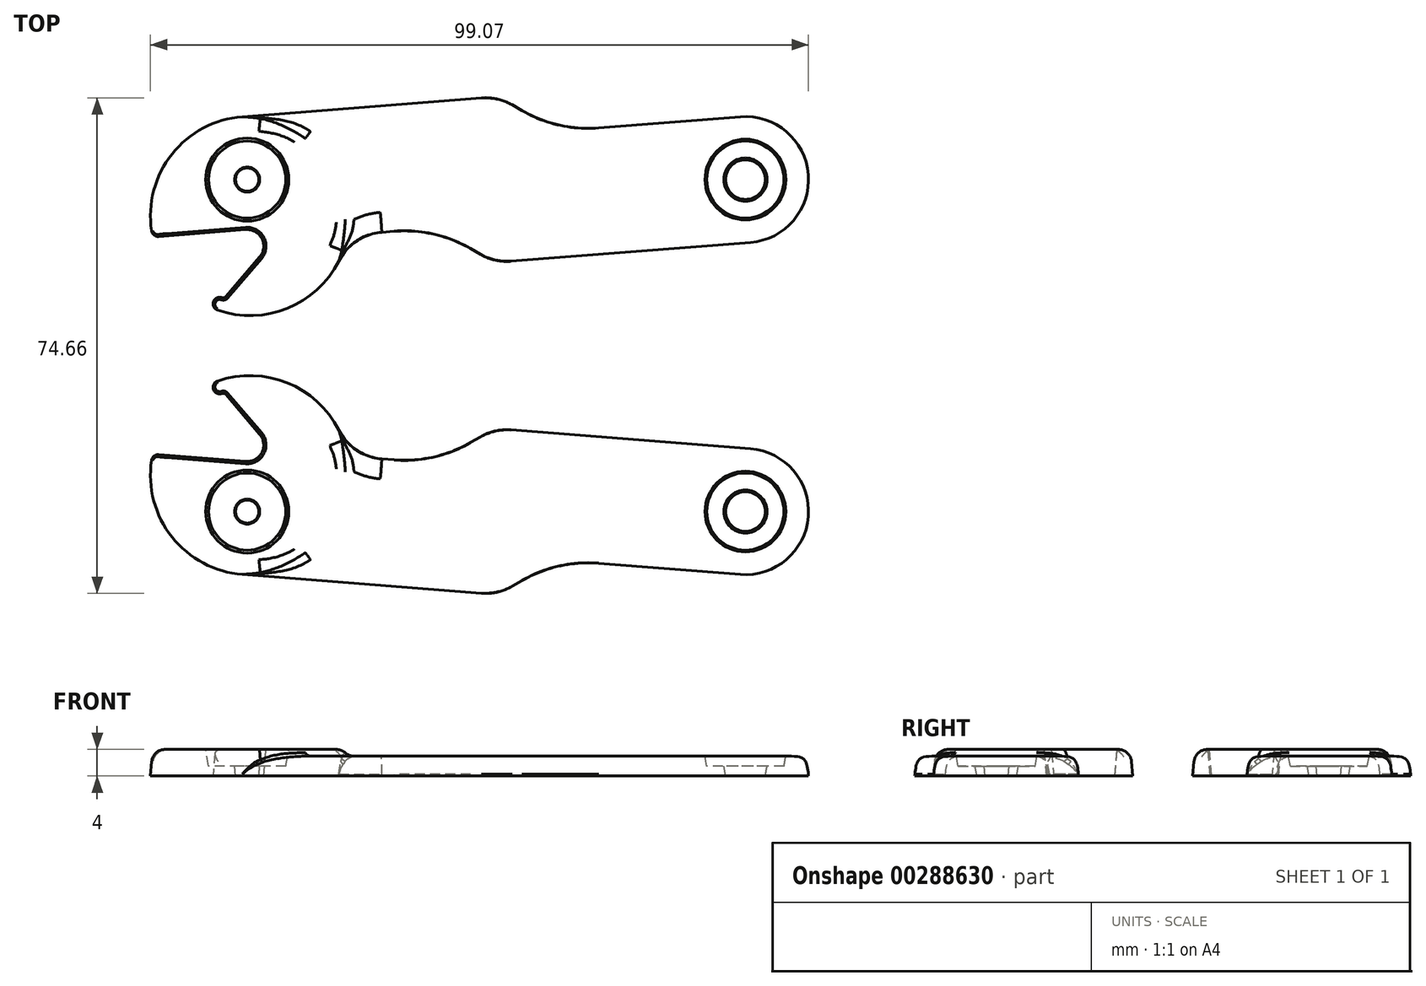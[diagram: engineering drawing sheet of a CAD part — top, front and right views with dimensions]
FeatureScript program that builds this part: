
annotation { "Feature Type Name" : "Feature", "Feature Type Description" : "" }
export const myFeature = defineFeature(function(context is Context, id is Id, definition is map)
    precondition{}
    {
        {
            var Q0;
            Q0=qCreatedBy(makeId("Top.planeOp"),FACE);
            var sketch = newSketch(context, id + "F0", { "sketchPlane" : qUnion([Q0])});
            skLineSegment(sketch, "E0", {"start": v(0, 0) * mm, "end": v(75, 0) * mm, "construction": true});
            skLineSegment(sketch, "E1", {"start": v(0, 0) * mm, "end": v(33, 2.6) * mm, "construction": true});
            skLineSegment(sketch, "E2", {"start": v(33, 2.6) * mm, "end": v(37.5, 0) * mm, "construction": true});
            skLineSegment(sketch, "E3", {"start": v(37.5, 0) * mm, "end": v(42, -2.6) * mm, "construction": true});
            skLineSegment(sketch, "E4", {"start": v(42, -2.6) * mm, "end": v(75, 0) * mm, "construction": true});
            skCircle(sketch, "E5", {"center": v(0, 0) * mm, "radius": 9.5 * mm, "construction": true});
            skArc(sketch, "E6", {"start": v(65.5, 0) * mm, "mid": v(81.98, -6.45) * mm, "end": v(74.25, 9.47) * mm});
            skLineSegment(sketch, "E7", {"start": v(-20.76, 0) * mm, "end": v(97.46, 0) * mm, "construction": true});
            skPoint(sketch, "E8", {"position": v(-9.5, 0) * mm});
            skPoint(sketch, "E9", {"position": v(84.5, 0) * mm});
            skLineSegment(sketch, "E10", {"start": v(0, 0) * mm, "end": v(-0.75, 9.47) * mm, "construction": true});
            skLineSegment(sketch, "E11", {"start": v(-0.75, 9.47) * mm, "end": v(37.75, 12.5) * mm});
            skLineSegment(sketch, "E12", {"start": v(37.75, 12.5) * mm, "end": v(46.74, 7.3) * mm});
            skLineSegment(sketch, "E13", {"start": v(46.74, 7.3) * mm, "end": v(74.25, 9.47) * mm});
            skLineSegment(sketch, "E14", {"start": v(0.75, -9.47) * mm, "end": v(28.26, -7.3) * mm});
            skLineSegment(sketch, "E15", {"start": v(28.26, -7.3) * mm, "end": v(37.25, -12.5) * mm});
            skLineSegment(sketch, "E16", {"start": v(37.25, -12.5) * mm, "end": v(75.75, -9.47) * mm});
            skLineSegment(sketch, "E17", {"start": v(37.75, 12.5) * mm, "end": v(28.26, -7.3) * mm, "construction": true});
            skLineSegment(sketch, "E18", {"start": v(46.74, 7.3) * mm, "end": v(37.25, -12.5) * mm, "construction": true});
            skCircle(sketch, "E19", {"center": v(0, 0) * mm, "radius": 1.75 * mm});
            skCircle(sketch, "E20", {"center": v(75, 0) * mm, "radius": 1.75 * mm});
            skLineSegment(sketch, "E21", {"start": v(0, 0) * mm, "end": v(1.6, -20.44) * mm, "construction": true});
            skArc(sketch, "E22", {"start": v(-0.75, 9.47) * mm, "mid": v(-11.32, 3.84) * mm, "end": v(-14.4, -7.73) * mm});
            skArc(sketch, "E23", {"start": v(1.6, -20.44) * mm, "mid": v(10.42, -16.67) * mm, "end": v(15.16, -8.34) * mm});
            skLineSegment(sketch, "E24", {"start": v(75, 0) * mm, "end": v(73.8, 15.34) * mm, "construction": true});
            skLineSegment(sketch, "E25", {"start": v(-3.23, -17.64) * mm, "end": v(1.88, -11.66) * mm});
            skLineSegment(sketch, "E26", {"start": v(-0.22, -7.54) * mm, "end": v(-13.33, -8.57) * mm});
            skLineSegment(sketch, "E27", {"start": v(-4.27, -18.86) * mm, "end": v(-6.06, -19) * mm, "construction": true});
            skArc(sketch, "E28", {"start": v(1.88, -11.66) * mm, "mid": v(2.2, -8.9) * mm, "end": v(-0.22, -7.54) * mm});
            skArc(sketch, "E29.trimOffspring", {"start": v(-4.47, -19.66) * mm, "mid": v(-1.47, -20.36) * mm, "end": v(1.6, -20.44) * mm});
            skPoint(sketch, "E30.visualSharp", {"position": v(-14.23, -8.64) * mm});
            skArc(sketch, "E30.filletArc", {"start": v(-14.4, -7.73) * mm, "mid": v(-14.03, -8.36) * mm, "end": v(-13.33, -8.57) * mm});
            skArc(sketch, "E31", {"start": v(-3.79, -17.78) * mm, "mid": v(-5.09, -18.37) * mm, "end": v(-4.47, -19.66) * mm});
            skArc(sketch, "E32.filletArc", {"start": v(-3.79, -17.78) * mm, "mid": v(-3.49, -17.8) * mm, "end": v(-3.23, -17.64) * mm});
            skSolve(sketch);
        }
        {
            var Q0;
            Q0=makeQuery(id+"F0.imprint","IMPRINT",FACE,{"disambiguationData":[TD([[makeQuery(id+"F0.imprint","IMPRINT",EDGE,{"derivedFrom":sQuery(id+"F0.wireOp",EDGE,"E19")}),-1.0]])]});
            var Q1;
            {var subQ6=sQuery(id+"F0.wireOp",EDGE,"E11");Q1=makeQuery(id+"F0.imprint","IMPRINT",FACE,{"disambiguationData":[TD([[makeQuery(id+"F0.imprint","IMPRINT",EDGE,{"derivedFrom":subQ6}),-1.0]])]});}
            var Q2;
            Q2=makeQuery(id+"F0.imprint","IMPRINT",FACE,{"disambiguationData":[TD([[makeQuery(id+"F0.imprint","IMPRINT",EDGE,{"derivedFrom":sQuery(id+"F0.wireOp",EDGE,"E20")}),-1.0]])]});
            var Q3;
            {var subQ1=sQuery(id+"F0.wireOp",EDGE,"E23");Q3=makeQuery(id+"F0.imprint","IMPRINT",FACE,{"disambiguationData":[TD([[makeQuery(id+"F0.imprint","IMPRINT",EDGE,{"derivedFrom":subQ1}),1.0]])]});}
            extrude(context, id + "F1", {"entities" : qUnion([Q0, Q1, Q2, Q3]), "depth" : 3 * mm, "hasDraft" : true, "draftAngle" : 5 * degree, "draftPullDirection" : true});
        }
        {
            var Q0;
            Q0=makeQuery(id+"F1.opExtrude","CAP_FACE",FACE,{"disambiguationData":[OSD([sQuery(id+"F0.wireOp",EDGE,"E6"),sQuery(id+"F0.wireOp",EDGE,"E11"),sQuery(id+"F0.wireOp",EDGE,"E12"),sQuery(id+"F0.wireOp",EDGE,"E13"),sQuery(id+"F0.wireOp",EDGE,"E14"),sQuery(id+"F0.wireOp",EDGE,"E15"),sQuery(id+"F0.wireOp",EDGE,"E16"),sQuery(id+"F0.wireOp",EDGE,"E19"),sQuery(id+"F0.wireOp",EDGE,"E20"),sQuery(id+"F0.wireOp",EDGE,"E22"),sQuery(id+"F0.wireOp",EDGE,"E23"),sQuery(id+"F0.wireOp",EDGE,"E25"),sQuery(id+"F0.wireOp",EDGE,"E26"),sQuery(id+"F0.wireOp",EDGE,"E28"),sQuery(id+"F0.wireOp",EDGE,"E29.trimOffspring"),sQuery(id+"F0.wireOp",EDGE,"E30.filletArc"),sQuery(id+"F0.wireOp",EDGE,"E31"),sQuery(id+"F0.wireOp",EDGE,"E32.filletArc")])],"isStart":false});
            var sketch = newSketch(context, id + "F2", { "sketchPlane" : qUnion([Q0])});
            skArc(sketch, "E33.0", {"start": v(-0.72, 9.2) * mm, "mid": v(-11.1, 3.68) * mm, "end": v(-14.14, -7.69) * mm});
            skArc(sketch, "E34.0", {"start": v(-14.14, -7.69) * mm, "mid": v(-13.87, -8.15) * mm, "end": v(-13.35, -8.31) * mm});
            skLineSegment(sketch, "E35.0", {"start": v(-0.24, -7.28) * mm, "end": v(-13.35, -8.31) * mm});
            skArc(sketch, "E36.0", {"start": v(2.08, -11.83) * mm, "mid": v(2.44, -8.78) * mm, "end": v(-0.24, -7.28) * mm});
            skLineSegment(sketch, "E37.0", {"start": v(-3.03, -17.8) * mm, "end": v(2.08, -11.83) * mm});
            skArc(sketch, "E38.0", {"start": v(-3.88, -18.02) * mm, "mid": v(-3.42, -18.05) * mm, "end": v(-3.03, -17.8) * mm});
            skArc(sketch, "E39.0", {"start": v(-3.88, -18.02) * mm, "mid": v(-4.84, -18.46) * mm, "end": v(-4.39, -19.41) * mm});
            skArc(sketch, "E40.0", {"start": v(-4.39, -19.41) * mm, "mid": v(7.88, -18.2) * mm, "end": v(14.94, -8.1) * mm});
            skArc(sketch, "E41", {"start": v(14.94, -8.1) * mm, "mid": v(11.36, 4.4) * mm, "end": v(-0.72, 9.2) * mm});
            skCircle(sketch, "E42.0", {"center": v(0, 0) * mm, "radius": 2.01 * mm});
            skSolve(sketch);
        }
        {
            var Q0;
            Q0=makeQuery(id+"F2.imprint","IMPRINT",FACE,{"disambiguationData":[TD([[makeQuery(id+"F2.imprint","IMPRINT",EDGE,{"derivedFrom":sQuery(id+"F2.wireOp",EDGE,"E33.0")}),1.0]])]});
            extrude(context, id + "F3", {"entities" : qUnion([Q0]), "operationType" : NewBodyOperationType.ADD, "depth" : 1 * mm, "hasDraft" : true, "draftAngle" : 5 * degree, "draftPullDirection" : true});
        }
        {
            var Q0;
            Q0=makeQuery(id+"F1.opExtrude","SWEPT_EDGE",EDGE,{"disambiguationData":[OSD([sQuery(id+"F0.wireOp",EDGE,"E14"),sQuery(id+"F0.wireOp",EDGE,"E15")])]});
            var Q1;
            Q1=makeQuery(id+"F1.opExtrude","SWEPT_EDGE",EDGE,{"disambiguationData":[OSD([sQuery(id+"F0.wireOp",EDGE,"E12"),sQuery(id+"F0.wireOp",EDGE,"E13")])]});
            fillet(context, id + "F4", {"entities" : qUnion([Q0, Q1]), "radius" : 20 * mm, "tangentPropagation" : true, "allowEdgeOverflow" : false});
        }
        {
            var Q0;
            Q0=makeQuery(id+"F1.opExtrude","SWEPT_EDGE",EDGE,{"disambiguationData":[OSD([sQuery(id+"F0.wireOp",EDGE,"E15"),sQuery(id+"F0.wireOp",EDGE,"SqaIxqJO-ytxu-bZqI-R6YT-mtZTRHwnqRUN")])]});
            var Q1;
            Q1=makeQuery(id+"F1.opExtrude","SWEPT_EDGE",EDGE,{"disambiguationData":[OSD([sQuery(id+"F0.wireOp",EDGE,"E15"),sQuery(id+"F0.wireOp",EDGE,"E16"),sQuery(id+"F0.wireOp",EDGE,"lhk9fa26-wqfy-sZaL-4qO0-kv8s20DjAP29")])]});
            var Q2;
            Q2=makeQuery(id+"F1.opExtrude","SWEPT_EDGE",EDGE,{"disambiguationData":[OSD([sQuery(id+"F0.wireOp",EDGE,"E11"),sQuery(id+"F0.wireOp",EDGE,"E12"),sQuery(id+"F0.wireOp",EDGE,"wIxREe3L-jgZz-AHNr-Kjfd-UXy7v7bFKsdN")])]});
            var Q3;
            Q3=makeQuery(id+"F1.opExtrude","SWEPT_EDGE",EDGE,{"disambiguationData":[OSD([sQuery(id+"F0.wireOp",EDGE,"E12"),sQuery(id+"F0.wireOp",EDGE,"acZJjbYW-XDDZ-AgQl-pZYt-mpwuyaKnzyxR")])]});
            var Q4;
            Q4=makeQuery(id+"F1.opExtrude","SWEPT_EDGE",EDGE,{"disambiguationData":[OSD([sQuery(id+"F0.wireOp",EDGE,"E14"),sQuery(id+"F0.wireOp",EDGE,"E23")])]});
            fillet(context, id + "F5", {"entities" : qUnion([Q0, Q1, Q2, Q3, Q4]), "radius" : 8 * mm, "tangentPropagation" : true, "allowEdgeOverflow" : false});
        }
        {
            var Q0;
            Q0=makeQuery(id+"F3.opExtrude","CAP_FACE",FACE,{"disambiguationData":[OSD([sQuery(id+"F2.wireOp",EDGE,"E33.0"),sQuery(id+"F2.wireOp",EDGE,"E34.0"),sQuery(id+"F2.wireOp",EDGE,"E35.0"),sQuery(id+"F2.wireOp",EDGE,"E36.0"),sQuery(id+"F2.wireOp",EDGE,"E37.0"),sQuery(id+"F2.wireOp",EDGE,"E38.0"),sQuery(id+"F2.wireOp",EDGE,"E39.0"),sQuery(id+"F2.wireOp",EDGE,"E40.0"),sQuery(id+"F2.wireOp",EDGE,"E41"),sQuery(id+"F2.wireOp",EDGE,"E42.0")])],"isStart":false});
            var sketch = newSketch(context, id + "F6", { "sketchPlane" : qUnion([Q0])});
            skCircle(sketch, "E43", {"center": v(0, 0) * mm, "radius": 3.5 * mm});
            skCircle(sketch, "E44", {"center": v(75, 0) * mm, "radius": 3.5 * mm});
            skLineSegment(sketch, "E45.bottom", {"start": v(-3, 3.5) * mm, "end": v(3, 3.5) * mm, "construction": true});
            skLineSegment(sketch, "E45.top", {"start": v(-3, -3.5) * mm, "end": v(3, -3.5) * mm, "construction": true});
            skLineSegment(sketch, "E45.left", {"start": v(-3, 3.5) * mm, "end": v(-3, -3.5) * mm});
            skLineSegment(sketch, "E45.right", {"start": v(3, 3.5) * mm, "end": v(3, -3.5) * mm});
            skLineSegment(sketch, "E46", {"start": v(-3, 3.5) * mm, "end": v(3, -3.5) * mm, "construction": true});
            skLineSegment(sketch, "E47.bottom", {"start": v(71.5, 3) * mm, "end": v(78.5, 3) * mm});
            skLineSegment(sketch, "E47.top", {"start": v(71.5, -3) * mm, "end": v(78.5, -3) * mm});
            skLineSegment(sketch, "E47.left", {"start": v(71.5, 3) * mm, "end": v(71.5, -3) * mm, "construction": true});
            skLineSegment(sketch, "E47.right", {"start": v(78.5, 3) * mm, "end": v(78.5, -3) * mm, "construction": true});
            skLineSegment(sketch, "E48", {"start": v(71.5, 3) * mm, "end": v(78.5, -3) * mm, "construction": true});
            skCircle(sketch, "E49.0", {"center": v(0, 0) * mm, "radius": 2.1 * mm});
            skSolve(sketch);
        }
        {
            var Q0;
            Q0=makeQuery(id+"F6.imprint","IMPRINT",FACE,{"disambiguationData":[TD([[makeQuery(id+"F6.imprint","IMPRINT",EDGE,{"derivedFrom":sQuery(id+"F6.wireOp",EDGE,"E49.0")}),-1.0]])]});
            var Q1;
            {var subQ0=sQuery(id+"F6.wireOp",EDGE,"E47.bottom");var subQ1=sQuery(id+"F6.wireOp",EDGE,"E44");var subQ2=makeQuery(id+"F6.imprint","INTERSECT",VERTEX,{"disambiguationData":[OD(0.0)],"derivedFrom":[subQ1,subQ0]});Q1=makeQuery(id+"F6.imprint","IMPRINT",FACE,{"disambiguationData":[TD([[makeQuery(id+"F6.imprint","IMPRINT",EDGE,{"disambiguationData":[TD([[subQ2,-1.0]])],"derivedFrom":subQ1}),1.0]])]});}
            extrude(context, id + "F7", {"entities" : qUnion([Q0, Q1]), "operationType" : NewBodyOperationType.REMOVE, "oppositeDirection" : true, "depth" : 2.5 * mm, "hasSecondDirection" : true, "secondDirectionBound" : SecondDirectionBoundingType.THROUGH_ALL, "secondDirectionOppositeDirection" : false, "secondDirectionDepth" : 25 * mm});
        }
        {
            var Q0;
            Q0=makeQuery(id+"F1.opExtrude","CAP_EDGE",EDGE,{"disambiguationData":[OSD([sQuery(id+"F0.wireOp",EDGE,"E14")])],"isStart":false});
            var Q1;
            Q1=makeQuery(id+"F1.opExtrude","CAP_EDGE",EDGE,{"disambiguationData":[OSD([sQuery(id+"F0.wireOp",EDGE,"E22")])],"isStart":false});
            var Q2;
            Q2=makeQuery(id+"F1.opExtrude","CAP_EDGE",EDGE,{"disambiguationData":[OSD([sQuery(id+"F0.wireOp",EDGE,"E11")])],"isStart":false});
            var Q3;
            {var subQ0=sQuery(id+"F0.wireOp",EDGE,"E12");var subQ1=sQuery(id+"F0.wireOp",EDGE,"E11");Q3=makeQuery(id+"F5.opFillet","BLEND_EDGE",EDGE,{"blendedFrom":[makeQuery(id+"F1.opExtrude","SWEPT_EDGE",EDGE,{"disambiguationData":[OSD([subQ1,subQ0])]}),makeQuery(id+"F1.opExtrude","CAP_FACE",FACE,{"disambiguationData":[OSD([sQuery(id+"F0.wireOp",EDGE,"E6"),subQ1,subQ0,sQuery(id+"F0.wireOp",EDGE,"E13"),sQuery(id+"F0.wireOp",EDGE,"E14"),sQuery(id+"F0.wireOp",EDGE,"E15"),sQuery(id+"F0.wireOp",EDGE,"E16"),sQuery(id+"F0.wireOp",EDGE,"E19"),sQuery(id+"F0.wireOp",EDGE,"E20"),sQuery(id+"F0.wireOp",EDGE,"E22"),sQuery(id+"F0.wireOp",EDGE,"E23"),sQuery(id+"F0.wireOp",EDGE,"E25"),sQuery(id+"F0.wireOp",EDGE,"E26"),sQuery(id+"F0.wireOp",EDGE,"E28"),sQuery(id+"F0.wireOp",EDGE,"E29.trimOffspring"),sQuery(id+"F0.wireOp",EDGE,"E30.filletArc"),sQuery(id+"F0.wireOp",EDGE,"E31"),sQuery(id+"F0.wireOp",EDGE,"E32.filletArc")])],"isStart":false})],"blendedInto":[makeQuery(id+"F1.opExtrude","CAP_FACE",FACE,{"disambiguationData":[OSD([sQuery(id+"F0.wireOp",EDGE,"E6"),subQ1,subQ0,sQuery(id+"F0.wireOp",EDGE,"E13"),sQuery(id+"F0.wireOp",EDGE,"E14"),sQuery(id+"F0.wireOp",EDGE,"E15"),sQuery(id+"F0.wireOp",EDGE,"E16"),sQuery(id+"F0.wireOp",EDGE,"E19"),sQuery(id+"F0.wireOp",EDGE,"E20"),sQuery(id+"F0.wireOp",EDGE,"E22"),sQuery(id+"F0.wireOp",EDGE,"E23"),sQuery(id+"F0.wireOp",EDGE,"E25"),sQuery(id+"F0.wireOp",EDGE,"E26"),sQuery(id+"F0.wireOp",EDGE,"E28"),sQuery(id+"F0.wireOp",EDGE,"E29.trimOffspring"),sQuery(id+"F0.wireOp",EDGE,"E30.filletArc"),sQuery(id+"F0.wireOp",EDGE,"E31"),sQuery(id+"F0.wireOp",EDGE,"E32.filletArc")])],"isStart":false})]});}
            var Q4;
            Q4=makeQuery(id+"F1.opExtrude","CAP_EDGE",EDGE,{"disambiguationData":[OSD([sQuery(id+"F0.wireOp",EDGE,"E12")])],"isStart":false});
            var Q5;
            {var subQ0=sQuery(id+"F0.wireOp",EDGE,"E13");var subQ1=sQuery(id+"F0.wireOp",EDGE,"E12");Q5=makeQuery(id+"F4.opFillet","BLEND_EDGE",EDGE,{"blendedFrom":[makeQuery(id+"F1.opExtrude","SWEPT_EDGE",EDGE,{"disambiguationData":[OSD([subQ1,subQ0])]}),makeQuery(id+"F1.opExtrude","CAP_FACE",FACE,{"disambiguationData":[OSD([sQuery(id+"F0.wireOp",EDGE,"E6"),sQuery(id+"F0.wireOp",EDGE,"E11"),subQ1,subQ0,sQuery(id+"F0.wireOp",EDGE,"E14"),sQuery(id+"F0.wireOp",EDGE,"E15"),sQuery(id+"F0.wireOp",EDGE,"E16"),sQuery(id+"F0.wireOp",EDGE,"E19"),sQuery(id+"F0.wireOp",EDGE,"E20"),sQuery(id+"F0.wireOp",EDGE,"E22"),sQuery(id+"F0.wireOp",EDGE,"E23"),sQuery(id+"F0.wireOp",EDGE,"E25"),sQuery(id+"F0.wireOp",EDGE,"E26"),sQuery(id+"F0.wireOp",EDGE,"E28"),sQuery(id+"F0.wireOp",EDGE,"E29.trimOffspring"),sQuery(id+"F0.wireOp",EDGE,"E30.filletArc"),sQuery(id+"F0.wireOp",EDGE,"E31"),sQuery(id+"F0.wireOp",EDGE,"E32.filletArc")])],"isStart":false})],"blendedInto":[makeQuery(id+"F1.opExtrude","CAP_FACE",FACE,{"disambiguationData":[OSD([sQuery(id+"F0.wireOp",EDGE,"E6"),sQuery(id+"F0.wireOp",EDGE,"E11"),subQ1,subQ0,sQuery(id+"F0.wireOp",EDGE,"E14"),sQuery(id+"F0.wireOp",EDGE,"E15"),sQuery(id+"F0.wireOp",EDGE,"E16"),sQuery(id+"F0.wireOp",EDGE,"E19"),sQuery(id+"F0.wireOp",EDGE,"E20"),sQuery(id+"F0.wireOp",EDGE,"E22"),sQuery(id+"F0.wireOp",EDGE,"E23"),sQuery(id+"F0.wireOp",EDGE,"E25"),sQuery(id+"F0.wireOp",EDGE,"E26"),sQuery(id+"F0.wireOp",EDGE,"E28"),sQuery(id+"F0.wireOp",EDGE,"E29.trimOffspring"),sQuery(id+"F0.wireOp",EDGE,"E30.filletArc"),sQuery(id+"F0.wireOp",EDGE,"E31"),sQuery(id+"F0.wireOp",EDGE,"E32.filletArc")])],"isStart":false})]});}
            var Q6;
            {var subQ0=sQuery(id+"F0.wireOp",EDGE,"E23");var subQ1=sQuery(id+"F0.wireOp",EDGE,"E14");Q6=makeQuery(id+"F5.opFillet","BLEND_EDGE",EDGE,{"blendedFrom":[makeQuery(id+"F1.opExtrude","SWEPT_EDGE",EDGE,{"disambiguationData":[OSD([subQ1,subQ0])]}),makeQuery(id+"F1.opExtrude","CAP_FACE",FACE,{"disambiguationData":[OSD([sQuery(id+"F0.wireOp",EDGE,"E6"),sQuery(id+"F0.wireOp",EDGE,"E11"),sQuery(id+"F0.wireOp",EDGE,"E12"),sQuery(id+"F0.wireOp",EDGE,"E13"),subQ1,sQuery(id+"F0.wireOp",EDGE,"E15"),sQuery(id+"F0.wireOp",EDGE,"E16"),sQuery(id+"F0.wireOp",EDGE,"E19"),sQuery(id+"F0.wireOp",EDGE,"E20"),sQuery(id+"F0.wireOp",EDGE,"E22"),subQ0,sQuery(id+"F0.wireOp",EDGE,"E25"),sQuery(id+"F0.wireOp",EDGE,"E26"),sQuery(id+"F0.wireOp",EDGE,"E28"),sQuery(id+"F0.wireOp",EDGE,"E29.trimOffspring"),sQuery(id+"F0.wireOp",EDGE,"E30.filletArc"),sQuery(id+"F0.wireOp",EDGE,"E31"),sQuery(id+"F0.wireOp",EDGE,"E32.filletArc")])],"isStart":false})],"blendedInto":[makeQuery(id+"F1.opExtrude","CAP_FACE",FACE,{"disambiguationData":[OSD([sQuery(id+"F0.wireOp",EDGE,"E6"),sQuery(id+"F0.wireOp",EDGE,"E11"),sQuery(id+"F0.wireOp",EDGE,"E12"),sQuery(id+"F0.wireOp",EDGE,"E13"),subQ1,sQuery(id+"F0.wireOp",EDGE,"E15"),sQuery(id+"F0.wireOp",EDGE,"E16"),sQuery(id+"F0.wireOp",EDGE,"E19"),sQuery(id+"F0.wireOp",EDGE,"E20"),sQuery(id+"F0.wireOp",EDGE,"E22"),subQ0,sQuery(id+"F0.wireOp",EDGE,"E25"),sQuery(id+"F0.wireOp",EDGE,"E26"),sQuery(id+"F0.wireOp",EDGE,"E28"),sQuery(id+"F0.wireOp",EDGE,"E29.trimOffspring"),sQuery(id+"F0.wireOp",EDGE,"E30.filletArc"),sQuery(id+"F0.wireOp",EDGE,"E31"),sQuery(id+"F0.wireOp",EDGE,"E32.filletArc")])],"isStart":false})]});}
            var Q7;
            {var subQ0=sQuery(id+"F0.wireOp",EDGE,"E15");var subQ1=sQuery(id+"F0.wireOp",EDGE,"E14");Q7=makeQuery(id+"F4.opFillet","BLEND_EDGE",EDGE,{"blendedFrom":[makeQuery(id+"F1.opExtrude","SWEPT_EDGE",EDGE,{"disambiguationData":[OSD([subQ1,subQ0])]}),makeQuery(id+"F1.opExtrude","CAP_FACE",FACE,{"disambiguationData":[OSD([sQuery(id+"F0.wireOp",EDGE,"E6"),sQuery(id+"F0.wireOp",EDGE,"E11"),sQuery(id+"F0.wireOp",EDGE,"E12"),sQuery(id+"F0.wireOp",EDGE,"E13"),subQ1,subQ0,sQuery(id+"F0.wireOp",EDGE,"E16"),sQuery(id+"F0.wireOp",EDGE,"E19"),sQuery(id+"F0.wireOp",EDGE,"E20"),sQuery(id+"F0.wireOp",EDGE,"E22"),sQuery(id+"F0.wireOp",EDGE,"E23"),sQuery(id+"F0.wireOp",EDGE,"E25"),sQuery(id+"F0.wireOp",EDGE,"E26"),sQuery(id+"F0.wireOp",EDGE,"E28"),sQuery(id+"F0.wireOp",EDGE,"E29.trimOffspring"),sQuery(id+"F0.wireOp",EDGE,"E30.filletArc"),sQuery(id+"F0.wireOp",EDGE,"E31"),sQuery(id+"F0.wireOp",EDGE,"E32.filletArc")])],"isStart":false})],"blendedInto":[makeQuery(id+"F1.opExtrude","CAP_FACE",FACE,{"disambiguationData":[OSD([sQuery(id+"F0.wireOp",EDGE,"E6"),sQuery(id+"F0.wireOp",EDGE,"E11"),sQuery(id+"F0.wireOp",EDGE,"E12"),sQuery(id+"F0.wireOp",EDGE,"E13"),subQ1,subQ0,sQuery(id+"F0.wireOp",EDGE,"E16"),sQuery(id+"F0.wireOp",EDGE,"E19"),sQuery(id+"F0.wireOp",EDGE,"E20"),sQuery(id+"F0.wireOp",EDGE,"E22"),sQuery(id+"F0.wireOp",EDGE,"E23"),sQuery(id+"F0.wireOp",EDGE,"E25"),sQuery(id+"F0.wireOp",EDGE,"E26"),sQuery(id+"F0.wireOp",EDGE,"E28"),sQuery(id+"F0.wireOp",EDGE,"E29.trimOffspring"),sQuery(id+"F0.wireOp",EDGE,"E30.filletArc"),sQuery(id+"F0.wireOp",EDGE,"E31"),sQuery(id+"F0.wireOp",EDGE,"E32.filletArc")])],"isStart":false})]});}
            var Q8;
            {var subQ0=sQuery(id+"F0.wireOp",EDGE,"E16");var subQ1=sQuery(id+"F0.wireOp",EDGE,"E15");Q8=makeQuery(id+"F5.opFillet","BLEND_EDGE",EDGE,{"blendedFrom":[makeQuery(id+"F1.opExtrude","SWEPT_EDGE",EDGE,{"disambiguationData":[OSD([subQ1,subQ0])]}),makeQuery(id+"F1.opExtrude","CAP_FACE",FACE,{"disambiguationData":[OSD([sQuery(id+"F0.wireOp",EDGE,"E6"),sQuery(id+"F0.wireOp",EDGE,"E11"),sQuery(id+"F0.wireOp",EDGE,"E12"),sQuery(id+"F0.wireOp",EDGE,"E13"),sQuery(id+"F0.wireOp",EDGE,"E14"),subQ1,subQ0,sQuery(id+"F0.wireOp",EDGE,"E19"),sQuery(id+"F0.wireOp",EDGE,"E20"),sQuery(id+"F0.wireOp",EDGE,"E22"),sQuery(id+"F0.wireOp",EDGE,"E23"),sQuery(id+"F0.wireOp",EDGE,"E25"),sQuery(id+"F0.wireOp",EDGE,"E26"),sQuery(id+"F0.wireOp",EDGE,"E28"),sQuery(id+"F0.wireOp",EDGE,"E29.trimOffspring"),sQuery(id+"F0.wireOp",EDGE,"E30.filletArc"),sQuery(id+"F0.wireOp",EDGE,"E31"),sQuery(id+"F0.wireOp",EDGE,"E32.filletArc")])],"isStart":false})],"blendedInto":[makeQuery(id+"F1.opExtrude","CAP_FACE",FACE,{"disambiguationData":[OSD([sQuery(id+"F0.wireOp",EDGE,"E6"),sQuery(id+"F0.wireOp",EDGE,"E11"),sQuery(id+"F0.wireOp",EDGE,"E12"),sQuery(id+"F0.wireOp",EDGE,"E13"),sQuery(id+"F0.wireOp",EDGE,"E14"),subQ1,subQ0,sQuery(id+"F0.wireOp",EDGE,"E19"),sQuery(id+"F0.wireOp",EDGE,"E20"),sQuery(id+"F0.wireOp",EDGE,"E22"),sQuery(id+"F0.wireOp",EDGE,"E23"),sQuery(id+"F0.wireOp",EDGE,"E25"),sQuery(id+"F0.wireOp",EDGE,"E26"),sQuery(id+"F0.wireOp",EDGE,"E28"),sQuery(id+"F0.wireOp",EDGE,"E29.trimOffspring"),sQuery(id+"F0.wireOp",EDGE,"E30.filletArc"),sQuery(id+"F0.wireOp",EDGE,"E31"),sQuery(id+"F0.wireOp",EDGE,"E32.filletArc")])],"isStart":false})]});}
            var Q9;
            Q9=makeQuery(id+"F1.opExtrude","CAP_EDGE",EDGE,{"disambiguationData":[OSD([sQuery(id+"F0.wireOp",EDGE,"E16")])],"isStart":false});
            var Q10;
            Q10=makeQuery(id+"F1.opExtrude","CAP_EDGE",EDGE,{"disambiguationData":[OSD([sQuery(id+"F0.wireOp",EDGE,"E6")])],"isStart":false});
            var Q11;
            Q11=makeQuery(id+"F1.opExtrude","CAP_EDGE",EDGE,{"disambiguationData":[OSD([sQuery(id+"F0.wireOp",EDGE,"E13")])],"isStart":false});
            var Q12;
            Q12=makeQuery(id+"F1.opExtrude","CAP_EDGE",EDGE,{"disambiguationData":[OSD([sQuery(id+"F0.wireOp",EDGE,"E15")])],"isStart":false});
            fillet(context, id + "F8", {"entities" : qUnion([Q0, Q1, Q2, Q3, Q4, Q5, Q6, Q7, Q8, Q9, Q10, Q11, Q12]), "radius" : 3 * mm, "rho" : 0.65, "crossSection" : FilletCrossSection.CONIC, "allowEdgeOverflow" : false});
        }
        {
            var Q0;
            Q0=makeQuery(id+"F3.opExtrude","CAP_EDGE",EDGE,{"disambiguationData":[OSD([sQuery(id+"F2.wireOp",EDGE,"E33.0"),sQuery(id+"F2.wireOp",EDGE,"E40.0"),sQuery(id+"F2.wireOp",EDGE,"E41")])],"isStart":false});
            fillet(context, id + "F9", {"entities" : qUnion([Q0]), "radius" : 2 * mm, "allowEdgeOverflow" : false});
        }
        {
            var Q0;
            {var subQ0=sQuery(id+"F0.wireOp",EDGE,"E29.trimOffspring");var subQ1=sQuery(id+"F0.wireOp",EDGE,"E23");var subQ2=sQuery(id+"F0.wireOp",EDGE,"E22");var subQ3=sQuery(id+"F0.wireOp",EDGE,"E14");Q0=makeQuery(id+"F8.opFillet","BLEND_EDGE",EDGE,{"blendedFrom":[makeQuery(id+"F5.opFillet","BLEND_EDGE",EDGE,{"blendedFrom":[makeQuery(id+"F1.opExtrude","SWEPT_EDGE",EDGE,{"disambiguationData":[OSD([subQ3,subQ1])]}),makeQuery(id+"F1.opExtrude","CAP_FACE",FACE,{"disambiguationData":[OSD([sQuery(id+"F0.wireOp",EDGE,"E6"),sQuery(id+"F0.wireOp",EDGE,"E11"),sQuery(id+"F0.wireOp",EDGE,"E12"),sQuery(id+"F0.wireOp",EDGE,"E13"),subQ3,sQuery(id+"F0.wireOp",EDGE,"E15"),sQuery(id+"F0.wireOp",EDGE,"E16"),sQuery(id+"F0.wireOp",EDGE,"E19"),sQuery(id+"F0.wireOp",EDGE,"E20"),subQ2,subQ1,sQuery(id+"F0.wireOp",EDGE,"E25"),sQuery(id+"F0.wireOp",EDGE,"E26"),sQuery(id+"F0.wireOp",EDGE,"E28"),subQ0,sQuery(id+"F0.wireOp",EDGE,"E30.filletArc"),sQuery(id+"F0.wireOp",EDGE,"E31"),sQuery(id+"F0.wireOp",EDGE,"E32.filletArc")])],"isStart":false})],"blendedInto":[makeQuery(id+"F1.opExtrude","CAP_FACE",FACE,{"disambiguationData":[OSD([sQuery(id+"F0.wireOp",EDGE,"E6"),sQuery(id+"F0.wireOp",EDGE,"E11"),sQuery(id+"F0.wireOp",EDGE,"E12"),sQuery(id+"F0.wireOp",EDGE,"E13"),subQ3,sQuery(id+"F0.wireOp",EDGE,"E15"),sQuery(id+"F0.wireOp",EDGE,"E16"),sQuery(id+"F0.wireOp",EDGE,"E19"),sQuery(id+"F0.wireOp",EDGE,"E20"),subQ2,subQ1,sQuery(id+"F0.wireOp",EDGE,"E25"),sQuery(id+"F0.wireOp",EDGE,"E26"),sQuery(id+"F0.wireOp",EDGE,"E28"),subQ0,sQuery(id+"F0.wireOp",EDGE,"E30.filletArc"),sQuery(id+"F0.wireOp",EDGE,"E31"),sQuery(id+"F0.wireOp",EDGE,"E32.filletArc")])],"isStart":false})]}),makeQuery(id+"F3.boolean.opBoolean","MERGE",FACE,{"derivedFrom":[makeQuery(id+"F1.opExtrude","SWEPT_FACE",FACE,{"disambiguationData":[OSD([subQ2])]}),makeQuery(id+"F1.opExtrude","SWEPT_FACE",FACE,{"disambiguationData":[OSD([subQ1,subQ0])]}),makeQuery(id+"F3.opExtrude","SWEPT_FACE",FACE,{"disambiguationData":[OSD([sQuery(id+"F2.wireOp",EDGE,"E33.0"),sQuery(id+"F2.wireOp",EDGE,"E40.0"),sQuery(id+"F2.wireOp",EDGE,"E41")])]})]})],"blendedInto":[makeQuery(id+"F3.boolean.opBoolean","MERGE",FACE,{"derivedFrom":[makeQuery(id+"F1.opExtrude","SWEPT_FACE",FACE,{"disambiguationData":[OSD([subQ2])]}),makeQuery(id+"F1.opExtrude","SWEPT_FACE",FACE,{"disambiguationData":[OSD([subQ1,subQ0])]}),makeQuery(id+"F3.opExtrude","SWEPT_FACE",FACE,{"disambiguationData":[OSD([sQuery(id+"F2.wireOp",EDGE,"E33.0"),sQuery(id+"F2.wireOp",EDGE,"E40.0"),sQuery(id+"F2.wireOp",EDGE,"E41")])]})]})]});}
            var Q1;
            Q1=makeQuery(id+"F9.opFillet","BLEND_EDGE",EDGE,{"blendedFrom":[makeQuery(id+"F3.opExtrude","CAP_EDGE",EDGE,{"disambiguationData":[OSD([sQuery(id+"F2.wireOp",EDGE,"E33.0"),sQuery(id+"F2.wireOp",EDGE,"E40.0"),sQuery(id+"F2.wireOp",EDGE,"E41")])],"isStart":false}),makeQuery(id+"F1.opExtrude","CAP_FACE",FACE,{"disambiguationData":[OSD([sQuery(id+"F0.wireOp",EDGE,"E6"),sQuery(id+"F0.wireOp",EDGE,"E11"),sQuery(id+"F0.wireOp",EDGE,"E12"),sQuery(id+"F0.wireOp",EDGE,"E13"),sQuery(id+"F0.wireOp",EDGE,"E14"),sQuery(id+"F0.wireOp",EDGE,"E15"),sQuery(id+"F0.wireOp",EDGE,"E16"),sQuery(id+"F0.wireOp",EDGE,"E19"),sQuery(id+"F0.wireOp",EDGE,"E20"),sQuery(id+"F0.wireOp",EDGE,"E22"),sQuery(id+"F0.wireOp",EDGE,"E23"),sQuery(id+"F0.wireOp",EDGE,"E25"),sQuery(id+"F0.wireOp",EDGE,"E26"),sQuery(id+"F0.wireOp",EDGE,"E28"),sQuery(id+"F0.wireOp",EDGE,"E29.trimOffspring"),sQuery(id+"F0.wireOp",EDGE,"E30.filletArc"),sQuery(id+"F0.wireOp",EDGE,"E31"),sQuery(id+"F0.wireOp",EDGE,"E32.filletArc")])],"isStart":false})],"blendedInto":[makeQuery(id+"F1.opExtrude","CAP_FACE",FACE,{"disambiguationData":[OSD([sQuery(id+"F0.wireOp",EDGE,"E6"),sQuery(id+"F0.wireOp",EDGE,"E11"),sQuery(id+"F0.wireOp",EDGE,"E12"),sQuery(id+"F0.wireOp",EDGE,"E13"),sQuery(id+"F0.wireOp",EDGE,"E14"),sQuery(id+"F0.wireOp",EDGE,"E15"),sQuery(id+"F0.wireOp",EDGE,"E16"),sQuery(id+"F0.wireOp",EDGE,"E19"),sQuery(id+"F0.wireOp",EDGE,"E20"),sQuery(id+"F0.wireOp",EDGE,"E22"),sQuery(id+"F0.wireOp",EDGE,"E23"),sQuery(id+"F0.wireOp",EDGE,"E25"),sQuery(id+"F0.wireOp",EDGE,"E26"),sQuery(id+"F0.wireOp",EDGE,"E28"),sQuery(id+"F0.wireOp",EDGE,"E29.trimOffspring"),sQuery(id+"F0.wireOp",EDGE,"E30.filletArc"),sQuery(id+"F0.wireOp",EDGE,"E31"),sQuery(id+"F0.wireOp",EDGE,"E32.filletArc")])],"isStart":false})]});
            fillet(context, id + "F10", {"entities" : qUnion([Q0, Q1]), "radius" : 2 * mm, "tangentPropagation" : true, "allowEdgeOverflow" : false});
        }
        {
            var Q0;
            Q0=qCreatedBy(makeId("Front.planeOp"),FACE);
            cPlane(context, id + "F11", {"entities" : qUnion([Q0]), "cplaneType" : CPlaneType.OFFSET, "offset" : 25 * mm, "width" : 150 * mm, "height" : 150 * mm});
        }
        {
            var Q0;
            Q0=makeQuery(id+"F3.opExtrude","CAP_FACE",FACE,{"disambiguationData":[OSD([sQuery(id+"F2.wireOp",EDGE,"E33.0"),sQuery(id+"F2.wireOp",EDGE,"E34.0"),sQuery(id+"F2.wireOp",EDGE,"E35.0"),sQuery(id+"F2.wireOp",EDGE,"E36.0"),sQuery(id+"F2.wireOp",EDGE,"E37.0"),sQuery(id+"F2.wireOp",EDGE,"E38.0"),sQuery(id+"F2.wireOp",EDGE,"E39.0"),sQuery(id+"F2.wireOp",EDGE,"E40.0"),sQuery(id+"F2.wireOp",EDGE,"E41"),sQuery(id+"F2.wireOp",EDGE,"E42.0")])],"isStart":false});
            var sketch = newSketch(context, id + "F12", { "sketchPlane" : qUnion([Q0])});
            skPoint(sketch, "E50.0", {"position": v(0, 0) * mm});
            skCircle(sketch, "E51.0", {"center": v(75, 0) * mm, "radius": 1.88 * mm});
            skCircle(sketch, "E52.0", {"center": v(0, 0) * mm, "radius": 1.75 * mm});
            skCircle(sketch, "E53", {"center": v(0, 0) * mm, "radius": 6.25 * mm});
            skCircle(sketch, "E54", {"center": v(75, 0) * mm, "radius": 6.25 * mm});
            skSolve(sketch);
        }
        {
            var Q0;
            Q0=makeQuery(id+"F12.imprint","IMPRINT",FACE,{"disambiguationData":[TD([[makeQuery(id+"F12.imprint","IMPRINT",EDGE,{"derivedFrom":sQuery(id+"F12.wireOp",EDGE,"E53")}),1.0]])]});
            var Q1;
            Q1=makeQuery(id+"F12.imprint","IMPRINT",FACE,{"disambiguationData":[TD([[makeQuery(id+"F12.imprint","IMPRINT",EDGE,{"derivedFrom":sQuery(id+"F12.wireOp",EDGE,"E51.0")}),-1.0]])]});
            var Q2;
            Q2=makeQuery(id+"F12.imprint","IMPRINT",FACE,{"disambiguationData":[TD([[makeQuery(id+"F12.imprint","IMPRINT",EDGE,{"derivedFrom":sQuery(id+"F12.wireOp",EDGE,"E52.0")}),-1.0]])]});
            var Q3;
            Q3=makeQuery(id+"F12.imprint","IMPRINT",FACE,{"disambiguationData":[TD([[makeQuery(id+"F12.imprint","IMPRINT",EDGE,{"derivedFrom":sQuery(id+"F12.wireOp",EDGE,"E52.0")}),1.0]])]});
            var Q4;
            Q4=makeQuery(id+"F12.imprint","IMPRINT",FACE,{"disambiguationData":[TD([[makeQuery(id+"F12.imprint","IMPRINT",EDGE,{"derivedFrom":sQuery(id+"F12.wireOp",EDGE,"E51.0")}),1.0]])]});
            var Q5;
            Q5=makeQuery(id+"F7.boolean.opBoolean","COPY",FACE,{"derivedFrom":makeQuery(id+"F7.opExtrude","CAP_FACE",FACE,{"disambiguationData":[OSD([sQuery(id+"F6.wireOp",EDGE,"E43"),sQuery(id+"F6.wireOp",EDGE,"E45.left"),sQuery(id+"F6.wireOp",EDGE,"E45.right"),sQuery(id+"F6.wireOp",EDGE,"E49.0")])],"isStart":false})});
            extrude(context, id + "F13", {"entities" : qUnion([Q0, Q1, Q2, Q3, Q4]), "operationType" : NewBodyOperationType.REMOVE, "endBound" : BoundingType.UP_TO_SURFACE, "oppositeDirection" : true, "endBoundEntityFace" : qUnion([Q5]), "depth" : 25 * mm, "hasDraft" : true, "draftAngle" : 10 * degree, "draftPullDirection" : true});
        }
        {
            var Q0;
            {var subQ0=sQuery(id+"F6.wireOp",EDGE,"E49.0");var subQ1=sQuery(id+"F6.wireOp",EDGE,"E45.right");var subQ2=sQuery(id+"F6.wireOp",EDGE,"E45.left");var subQ3=sQuery(id+"F6.wireOp",EDGE,"E43");Q0=makeQuery(id+"F13.boolean.opBoolean","MERGE",FACE,{"derivedFrom":[makeQuery(id+"F7.boolean.opBoolean","COPY",FACE,{"derivedFrom":makeQuery(id+"F7.opExtrude","CAP_FACE",FACE,{"disambiguationData":[OSD([subQ3,subQ2,subQ1,subQ0])],"isStart":false})}),makeQuery(id+"F13.opExtrude","CAP_FACE",FACE,{"disambiguationData":[OSD([subQ3,subQ2,subQ1,subQ0]),ownerDisambiguation([makeQuery(id+"F12.imprint","IMPRINT",EDGE,{"derivedFrom":sQuery(id+"F12.wireOp",EDGE,"E53")})])],"isStart":false})]});}
            var sketch = newSketch(context, id + "F14", { "sketchPlane" : qUnion([Q0])});
            skPoint(sketch, "E55.0", {"position": v(0, 0) * mm});
            skCircle(sketch, "E56.0", {"center": v(75, 0) * mm, "radius": 1.88 * mm});
            skCircle(sketch, "E57.0.0", {"center": v(75, 0) * mm, "radius": 5.8 * mm});
            skCircle(sketch, "E58.0", {"center": v(0, 0) * mm, "radius": 1.75 * mm});
            skCircle(sketch, "E59", {"center": v(0, 0) * mm, "radius": 3.25 * mm});
            skCircle(sketch, "E60", {"center": v(75, 0) * mm, "radius": 3.25 * mm});
            skSolve(sketch);
        }
        {
            var Q0;
            Q0=makeQuery(id+"F14.imprint","IMPRINT",FACE,{"disambiguationData":[TD([[makeQuery(id+"F14.imprint","IMPRINT",EDGE,{"derivedFrom":sQuery(id+"F14.wireOp",EDGE,"E58.0")}),-1.0]])]});
            var Q1;
            Q1=makeQuery(id+"F14.imprint","IMPRINT",FACE,{"disambiguationData":[TD([[makeQuery(id+"F14.imprint","IMPRINT",EDGE,{"derivedFrom":sQuery(id+"F14.wireOp",EDGE,"E56.0")}),-1.0]])]});
            var Q2;
            Q2=makeQuery(id+"F14.imprint","IMPRINT",FACE,{"disambiguationData":[TD([[makeQuery(id+"F14.imprint","IMPRINT",EDGE,{"derivedFrom":sQuery(id+"F14.wireOp",EDGE,"E58.0")}),1.0]])]});
            var Q3;
            Q3=makeQuery(id+"F14.imprint","IMPRINT",FACE,{"disambiguationData":[TD([[makeQuery(id+"F14.imprint","IMPRINT",EDGE,{"derivedFrom":sQuery(id+"F14.wireOp",EDGE,"E56.0")}),1.0]])]});
            extrude(context, id + "F15", {"entities" : qUnion([Q0, Q1, Q2, Q3]), "operationType" : NewBodyOperationType.REMOVE, "endBound" : BoundingType.THROUGH_ALL, "oppositeDirection" : true, "depth" : 25 * mm, "hasDraft" : true, "draftAngle" : 10 * degree, "draftPullDirection" : true});
        }
        {
            var Q0;
            Q0=makeQuery(id+"F1.opExtrude","SWEPT_BODY",BODY,{"disambiguationData":[OSD([sQuery(id+"F0.wireOp",EDGE,"E5"),sQuery(id+"F0.wireOp",EDGE,"E6"),sQuery(id+"F0.wireOp",EDGE,"E11"),sQuery(id+"F0.wireOp",EDGE,"E12"),sQuery(id+"F0.wireOp",EDGE,"E13"),sQuery(id+"F0.wireOp",EDGE,"E14"),sQuery(id+"F0.wireOp",EDGE,"E15"),sQuery(id+"F0.wireOp",EDGE,"E16"),sQuery(id+"F0.wireOp",EDGE,"wIxREe3L-jgZz-AHNr-Kjfd-UXy7v7bFKsdN"),sQuery(id+"F0.wireOp",EDGE,"acZJjbYW-XDDZ-AgQl-pZYt-mpwuyaKnzyxR"),sQuery(id+"F0.wireOp",EDGE,"8jvX9M8M-g9B3-7RFz-hZYw-rqmUKc7UIlDm"),sQuery(id+"F0.wireOp",EDGE,"SqaIxqJO-ytxu-bZqI-R6YT-mtZTRHwnqRUN"),sQuery(id+"F0.wireOp",EDGE,"lhk9fa26-wqfy-sZaL-4qO0-kv8s20DjAP29"),sQuery(id+"F0.wireOp",EDGE,"lR5X3Id9-I5ne-W4Mq-rIuh-GVdJCYzghld6"),sQuery(id+"F0.wireOp",EDGE,"iDbUJSfV-XE6g-bhuF-RKb2-MMIm4VSMwOz5"),sQuery(id+"F0.wireOp",EDGE,"E19"),sQuery(id+"F0.wireOp",EDGE,"E20"),sQuery(id+"F0.wireOp",EDGE,"7kF2NE7P-aKSG-3UDD-ZtTx-ptxEGAuk2JOO")])]});
            var Q1;
            Q1=qCreatedBy(id+"F11.planeOp",FACE);
            mirror(context, id + "F16", {"entities" : qUnion([Q0]), "mirrorPlane" : qUnion([Q1])});
        }
    });
